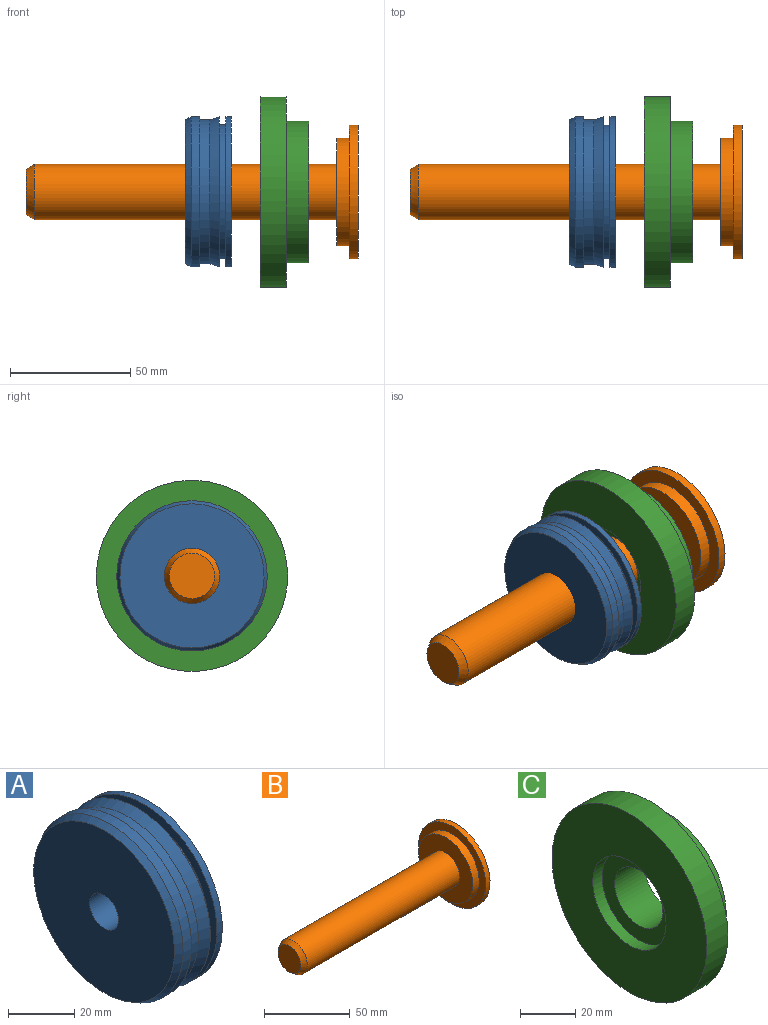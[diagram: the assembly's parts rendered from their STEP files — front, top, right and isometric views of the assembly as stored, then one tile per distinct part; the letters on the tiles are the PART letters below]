
ASSEMBLY  parts=3 mates=2
PART A: 14 faces, bbox 19.1x62.5x62.5 mm
  f0: plane 19.12x19.12mm, normal (1,0,0), area 168mm2, adj f1,f13
  f1: cylinder r=9.56mm len=19.12mm, axis (-1,0,0), area 204.3mm2, adj f0,f2
  f2: plane 62.54x62.54mm, normal (1,0,0), area 2784.5mm2, adj f1,f3
  f3: cylinder r=31.27mm len=62.54mm, axis (-1,0,0), area 445.6mm2, adj f2,f4
  f4: plane 62.54x62.54mm, normal (-1,0,0), area 637.8mm2, adj f3,f5
  f5: cylinder r=27.83mm len=55.67mm, axis (-1,0,0), area 487.2mm2, adj f4,f6
  f6: plane 62.54x62.54mm, normal (1,0,0), area 637.8mm2, adj f5,f7
  f7: cone r=31.27mm half-angle=18.4deg, axis (1,0,0), area 788.5mm2, adj f6,f8
  f8: cylinder r=29.97mm len=59.94mm, axis (-1,0,0), area 787.3mm2, adj f7,f9
  f9: plane 62.54x62.54mm, normal (1,0,0), area 249.4mm2, adj f8,f10
  f10: cylinder r=31.27mm len=62.54mm, axis (-1,0,0), area 700.2mm2, adj f9,f11
  f11: cone r=31.27mm half-angle=28.1deg, axis (1,0,0), area 529.9mm2, adj f10,f12
  f12: plane 59.94x59.94mm, normal (-1,0,0), area 2703.1mm2, adj f11,f13
  f13: cylinder r=6.16mm len=15.72mm, axis (-1,0,0), area 607.9mm2, adj f0,f12
PART B: 8 faces, bbox 138.1x55.6x55.6 mm
  f0: plane 55.64x55.64mm, normal (1,0,0), area 2431.5mm2, adj f7
  f1: plane 18.83x18.83mm, normal (-1,0,0), area 278.4mm2, adj f2
  f2: cone r=9.41mm half-angle=32deg, axis (1,0,0), area 259.4mm2, adj f1,f3
  f3: cylinder r=11.5mm len=125.92mm, axis (1,0,0), area 9102.6mm2, adj f2,f4
  f4: plane 44.76x44.76mm, normal (-1,0,0), area 1158mm2, adj f3,f5
  f5: cylinder r=22.38mm len=44.76mm, axis (1,0,0), area 735.4mm2, adj f4,f6
  f6: plane 55.64x55.64mm, normal (-1,0,0), area 857.7mm2, adj f5,f7
  f7: cylinder r=27.82mm len=55.64mm, axis (1,0,0), area 621.6mm2, adj f0,f6
PART C: 8 faces, bbox 20.2x79.5x79.5 mm
  f0: plane 37.65x37.65mm, normal (-1,0,0), area 634.9mm2, adj f1,f7
  f1: cylinder r=12.34mm len=24.68mm, axis (1,0,0), area 1192.2mm2, adj f0,f2
  f2: plane 58.99x58.99mm, normal (1,0,0), area 2254.3mm2, adj f1,f3
  f3: cylinder r=29.49mm len=58.99mm, axis (1,0,0), area 1725mm2, adj f2,f4
  f4: plane 79.49x79.49mm, normal (1,0,0), area 2229.4mm2, adj f3,f5
  f5: cylinder r=39.74mm len=79.49mm, axis (1,0,0), area 2716.2mm2, adj f4,f6
  f6: plane 79.49x79.49mm, normal (-1,0,0), area 3848.8mm2, adj f5,f7
  f7: cylinder r=18.83mm len=37.65mm, axis (1,0,0), area 569.1mm2, adj f0,f6
PLACE A t=(-62.44,0,14.82)mm
PLACE B t=(-36.06,0,14.82)mm
PLACE C t=(-30.32,0,14.82)mm
MATE cylindrical B.f2 <-> C.f1  axis (1,0,0) through (-81.56,0,14.82)mm
MATE cylindrical B.f2 <-> A.f1  axis (1,0,0) through (-81.56,0,14.82)mm
